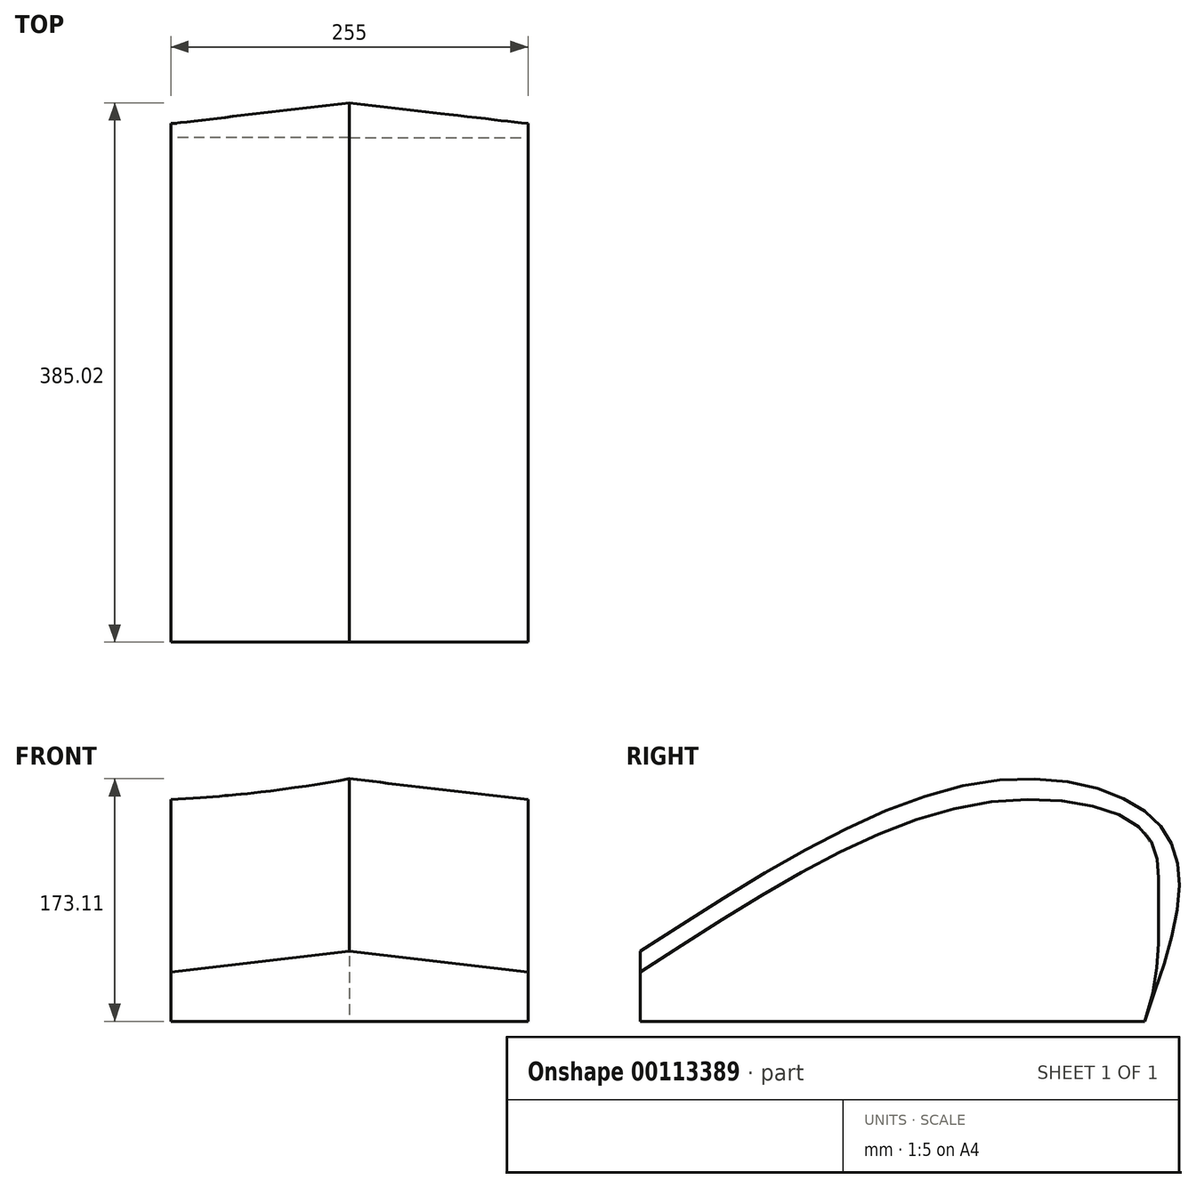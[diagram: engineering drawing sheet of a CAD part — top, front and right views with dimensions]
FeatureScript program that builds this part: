
annotation { "Feature Type Name" : "Feature", "Feature Type Description" : "" }
export const myFeature = defineFeature(function(context is Context, id is Id, definition is map)
    precondition{}
    {
        {
            var Q0;
            Q0=qCreatedBy(makeId("Front.planeOp"),FACE);
            cPlane(context, id + "F0", {"entities" : qUnion([Q0]), "cplaneType" : CPlaneType.OFFSET, "offset" : 240 * mm, "oppositeDirection" : true, "width" : 150 * mm, "height" : 150 * mm});
        }
        {
            var Q0;
            Q0=qCreatedBy(id+"F0.planeOp",FACE);
            cPlane(context, id + "F1", {"entities" : qUnion([Q0]), "cplaneType" : CPlaneType.OFFSET, "offset" : 120 * mm, "oppositeDirection" : true, "width" : 150 * mm, "height" : 150 * mm});
        }
        {
            var Q0;
            Q0=qCreatedBy(id+"F1.planeOp",FACE);
            cPlane(context, id + "F2", {"entities" : qUnion([Q0]), "cplaneType" : CPlaneType.OFFSET, "offset" : 25 * mm, "oppositeDirection" : true, "width" : 150 * mm, "height" : 150 * mm});
        }
        {
            var Q0;
            Q0=qCreatedBy(makeId("Right.planeOp"),FACE);
            var sketch = newSketch(context, id + "F3", { "sketchPlane" : qUnion([Q0])});
            skLineSegment(sketch, "E0", {"start": v(0, 0) * mm, "end": v(0, 50) * mm, "construction": true});
            skLineSegment(sketch, "E1", {"start": v(0, 0) * mm, "end": v(385, 0) * mm, "construction": true});
            skLineSegment(sketch, "E2", {"start": v(240, 0) * mm, "end": v(240, 170) * mm, "construction": true});
            skLineSegment(sketch, "E3", {"start": v(385, 0) * mm, "end": v(385, 100) * mm, "construction": true});
            skLineSegment(sketch, "E4", {"start": v(360, 0) * mm, "end": v(360, 150) * mm, "construction": true});
            skLineSegment(sketch, "E5", {"start": v(0, 50) * mm, "end": v(0, 0) * mm});
            skLineSegment(sketch, "E6", {"start": v(0, 0) * mm, "end": v(360, 0) * mm});
            skFitSpline(sketch, "E7", {"points": [v(0, 50) * mm, v(240, 170) * mm, v(360, 150) * mm, v(385, 100) * mm, v(360, 0) * mm], "startDerivative": vector(685.87, 442.37) * mm, "endDerivative": vector(-170.01, -477.73) * mm});
            skSolve(sketch);
        }
        {
            var Q0;
            Q0=qCreatedBy(makeId("Right.planeOp"),FACE);
            cPlane(context, id + "F4", {"entities" : qUnion([Q0]), "cplaneType" : CPlaneType.OFFSET, "offset" : 127.5 * mm, "width" : 150 * mm, "height" : 150 * mm});
        }
        {
            var Q0;
            Q0=qCreatedBy(id+"F4.planeOp",FACE);
            var sketch = newSketch(context, id + "F5", { "sketchPlane" : qUnion([Q0])});
            skLineSegment(sketch, "E8", {"start": v(0, 0) * mm, "end": v(0, 35) * mm, "construction": true});
            skLineSegment(sketch, "E9", {"start": v(0, 0) * mm, "end": v(370, 0) * mm, "construction": true});
            skLineSegment(sketch, "E10", {"start": v(240, 0) * mm, "end": v(240, 155) * mm, "construction": true});
            skLineSegment(sketch, "E11", {"start": v(370, 0) * mm, "end": v(370, 85) * mm, "construction": true});
            skLineSegment(sketch, "E12", {"start": v(360, 0) * mm, "end": v(360, 135) * mm, "construction": true});
            skLineSegment(sketch, "E13", {"start": v(0, 35) * mm, "end": v(0, 0) * mm});
            skLineSegment(sketch, "E14", {"start": v(0, 0) * mm, "end": v(360, 0) * mm});
            skFitSpline(sketch, "E15", {"points": [v(0, 35) * mm, v(240, 155) * mm, v(360, 135) * mm, v(370, 85) * mm, v(360, 0) * mm], "startDerivative": vector(685.87, 442.37) * mm, "endDerivative": vector(-170.01, -477.73) * mm});
            skSolve(sketch);
        }
        {
            var Q0;
            Q0=makeQuery(id+"F3.imprint","IMPRINT",FACE,{"disambiguationData":[TD([[makeQuery(id+"F3.imprint","IMPRINT",EDGE,{"derivedFrom":sQuery(id+"F3.wireOp",EDGE,"E5")}),1.0]])]});
            var Q1;
            Q1=makeQuery(id+"F5.imprint","IMPRINT",FACE,{"disambiguationData":[TD([[makeQuery(id+"F5.imprint","IMPRINT",EDGE,{"derivedFrom":sQuery(id+"F5.wireOp",EDGE,"E13")}),1.0]])]});
            loft(context, id + "F6", {"sheetProfilesArray" : [{ "sheetProfileEntities" : qUnion([Q0]) }, { "sheetProfileEntities" : qUnion([Q1]) }]});
        }
        {
            var Q0;
            Q0=qCreatedBy(makeId("Right.planeOp"),FACE);
            cPlane(context, id + "F7", {"entities" : qUnion([Q0]), "cplaneType" : CPlaneType.OFFSET, "offset" : 127.5 * mm, "oppositeDirection" : true, "width" : 150 * mm, "height" : 150 * mm});
        }
        {
            var Q0;
            Q0=qCreatedBy(id+"F7.planeOp",FACE);
            var sketch = newSketch(context, id + "F8", { "sketchPlane" : qUnion([Q0])});
            skLineSegment(sketch, "E16", {"start": v(0, 0) * mm, "end": v(0, 35) * mm, "construction": true});
            skLineSegment(sketch, "E17", {"start": v(0, 0) * mm, "end": v(370, 0) * mm, "construction": true});
            skLineSegment(sketch, "E18", {"start": v(240, 0) * mm, "end": v(240, 155) * mm, "construction": true});
            skLineSegment(sketch, "E19", {"start": v(370, 0) * mm, "end": v(370, 85) * mm, "construction": true});
            skLineSegment(sketch, "E20", {"start": v(360, 0) * mm, "end": v(360, 135) * mm, "construction": true});
            skLineSegment(sketch, "E21", {"start": v(0, 35) * mm, "end": v(0, 0) * mm});
            skLineSegment(sketch, "E22", {"start": v(0, 0) * mm, "end": v(360, 0) * mm});
            skFitSpline(sketch, "E23", {"points": [v(0, 35) * mm, v(240, 155) * mm, v(360, 135) * mm, v(370, 85) * mm, v(360, 0) * mm], "startDerivative": vector(685.87, 442.37) * mm, "endDerivative": vector(-170.01, -477.73) * mm});
            skSolve(sketch);
        }
        {
            var Q1;
            Q1=makeQuery(id+"F6.opLoft","CAP_FACE",FACE,{"disambiguationData":[OSD([makeQuery(id+"F3.imprint","IMPRINT",FACE,{"disambiguationData":[TD([[makeQuery(id+"F3.imprint","IMPRINT",EDGE,{"derivedFrom":sQuery(id+"F3.wireOp",EDGE,"E5")}),1.0]])]})])],"isStart":true});
            var Q2;
            Q2=makeQuery(id+"F8.imprint","IMPRINT",FACE,{"disambiguationData":[TD([[makeQuery(id+"F8.imprint","IMPRINT",EDGE,{"derivedFrom":sQuery(id+"F8.wireOp",EDGE,"E21")}),1.0]])]});
            loft(context, id + "F9", {"operationType" : NewBodyOperationType.ADD, "sheetProfilesArray" : [{ "sheetProfileEntities" : qUnion([Q1]) }, { "sheetProfileEntities" : qUnion([Q2]) }]});
        }
    });
